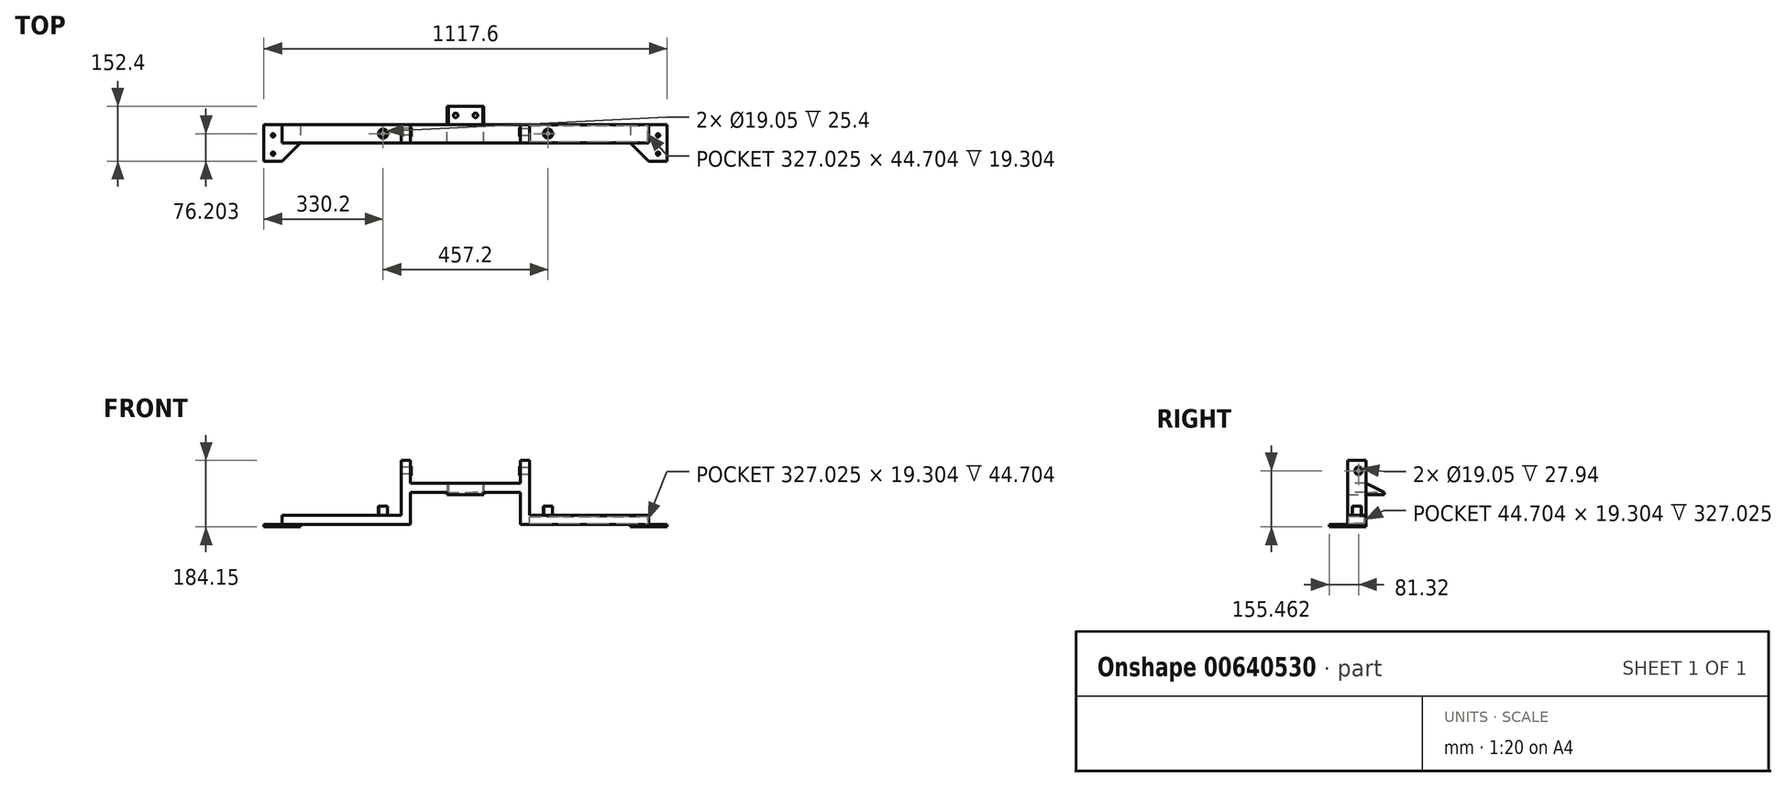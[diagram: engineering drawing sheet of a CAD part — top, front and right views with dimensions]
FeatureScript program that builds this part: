
annotation { "Feature Type Name" : "Feature", "Feature Type Description" : "" }
export const myFeature = defineFeature(function(context is Context, id is Id, definition is map)
    precondition{}
    {
        {
            var Q0;
            Q0=qCreatedBy(makeId("Top.planeOp"),FACE);
            var sketch = newSketch(context, id + "F0", { "sketchPlane" : qUnion([Q0])});
            skLineSegment(sketch, "E0.bottom", {"start": v(0, 37.2) * mm, "end": v(355.6, 37.2) * mm});
            skLineSegment(sketch, "E0.top", {"start": v(0, -13.6) * mm, "end": v(355.6, -13.6) * mm});
            skLineSegment(sketch, "E0.left", {"start": v(0, 37.2) * mm, "end": v(0, -13.6) * mm});
            skLineSegment(sketch, "E0.right", {"start": v(355.6, 37.2) * mm, "end": v(355.6, -13.6) * mm});
            skSolve(sketch);
        }
        {
            var Q0;
            Q0=makeQuery(id+"F0.imprint","IMPRINT",FACE,{"disambiguationData":[TD([[makeQuery(id+"F0.imprint","IMPRINT",EDGE,{"derivedFrom":sQuery(id+"F0.wireOp",EDGE,"E0.bottom")}),-1.0]])]});
            extrude(context, id + "F1", {"entities" : qUnion([Q0]), "depth" : 25.4 * mm, "offsetDistance" : 25.4 * mm});
        }
        {
            var Q0;
            Q0=qCreatedBy(makeId("Top.planeOp"),FACE);
            var sketch = newSketch(context, id + "F2", { "sketchPlane" : qUnion([Q0])});
            skLineSegment(sketch, "E1.0", {"start": v(0, 37.2) * mm, "end": v(355.6, 37.2) * mm});
            skLineSegment(sketch, "E2.0", {"start": v(0, -13.6) * mm, "end": v(355.6, -13.6) * mm});
            skLineSegment(sketch, "E3", {"start": v(304.8, -13.6) * mm, "end": v(355.6, -64.4) * mm});
            skLineSegment(sketch, "E4", {"start": v(355.6, -64.4) * mm, "end": v(406.4, -64.4) * mm});
            skLineSegment(sketch, "E5", {"start": v(406.4, -64.4) * mm, "end": v(406.4, 37.2) * mm});
            skLineSegment(sketch, "E6", {"start": v(406.4, 37.2) * mm, "end": v(304.8, 37.2) * mm});
            skLineSegment(sketch, "E7", {"start": v(304.8, 37.2) * mm, "end": v(304.8, -13.6) * mm});
            skSolve(sketch);
        }
        {
            var Q0;
            Q0=qSketchRegion(id+"F2",true);
            extrude(context, id + "F3", {"entities" : qUnion([Q0]), "operationType" : NewBodyOperationType.ADD, "oppositeDirection" : true, "depth" : 6.35 * mm, "offsetDistance" : 25.4 * mm});
        }
        {
            var Q0;
            Q0=makeQuery(id+"F3.opExtrude","CAP_FACE",FACE,{"disambiguationData":[OSD([sQuery(id+"F2.wireOp",EDGE,"E3"),sQuery(id+"F2.wireOp",EDGE,"E4"),sQuery(id+"F2.wireOp",EDGE,"E5"),sQuery(id+"F2.wireOp",EDGE,"E6"),sQuery(id+"F2.wireOp",EDGE,"E7")])],"isStart":true});
            var sketch = newSketch(context, id + "F4", { "sketchPlane" : qUnion([Q0])});
            skCircle(sketch, "E8", {"center": v(381, -43.77) * mm, "radius": 4.76 * mm});
            skCircle(sketch, "E9", {"center": v(381, 7.03) * mm, "radius": 4.76 * mm});
            skSolve(sketch);
        }
        {
            var Q0;
            Q0=qSketchRegion(id+"F4",true);
            extrude(context, id + "F5", {"entities" : qUnion([Q0]), "operationType" : NewBodyOperationType.REMOVE, "oppositeDirection" : true, "depth" : 25.4 * mm, "offsetDistance" : 25.4 * mm});
        }
        {
            var Q0;
            Q0=makeQuery(id+"F1.opExtrude","CAP_FACE",FACE,{"disambiguationData":[OSD([sQuery(id+"F0.wireOp",EDGE,"E0.bottom"),sQuery(id+"F0.wireOp",EDGE,"E0.top"),sQuery(id+"F0.wireOp",EDGE,"E0.left"),sQuery(id+"F0.wireOp",EDGE,"E0.right")])],"isStart":false});
            var sketch = newSketch(context, id + "F6", { "sketchPlane" : qUnion([Q0])});
            skCircle(sketch, "E10", {"center": v(76.2, 11.8) * mm, "radius": 12.7 * mm});
            skCircle(sketch, "E11", {"center": v(76.2, 11.8) * mm, "radius": 9.53 * mm});
            skSolve(sketch);
        }
        {
            var Q0;
            Q0=makeQuery(id+"F6.imprint","IMPRINT",FACE,{"disambiguationData":[TD([[makeQuery(id+"F6.imprint","IMPRINT",EDGE,{"derivedFrom":sQuery(id+"F6.wireOp",EDGE,"E10")}),1.0]])]});
            var Q1;
            Q1=sQuery(id+"F6.wireOp",EDGE,"E10");
            var Q2;
            Q2=sQuery(id+"F6.wireOp",EDGE,"E11");
            extrude(context, id + "F7", {"entities" : qUnion([Q0]), "operationType" : NewBodyOperationType.ADD, "surfaceEntities" : qUnion([Q1, Q2]), "depth" : 25.4 * mm, "offsetDistance" : 25.4 * mm});
        }
        {
            var Q0;
            Q0=makeQuery(id+"F1.opExtrude","CAP_FACE",FACE,{"disambiguationData":[OSD([sQuery(id+"F0.wireOp",EDGE,"E0.bottom"),sQuery(id+"F0.wireOp",EDGE,"E0.top"),sQuery(id+"F0.wireOp",EDGE,"E0.left"),sQuery(id+"F0.wireOp",EDGE,"E0.right")])],"isStart":false});
            var sketch = newSketch(context, id + "F8", { "sketchPlane" : qUnion([Q0])});
            skLineSegment(sketch, "E12.bottom", {"start": v(0, 37.2) * mm, "end": v(25.4, 37.2) * mm});
            skLineSegment(sketch, "E12.top", {"start": v(0, -13.6) * mm, "end": v(25.4, -13.6) * mm});
            skLineSegment(sketch, "E12.left", {"start": v(0, 37.2) * mm, "end": v(0, -13.6) * mm});
            skLineSegment(sketch, "E12.right", {"start": v(25.4, 37.2) * mm, "end": v(25.4, -13.6) * mm});
            skSolve(sketch);
        }
        {
            var Q0;
            Q0=qSketchRegion(id+"F8",true);
            extrude(context, id + "F9", {"entities" : qUnion([Q0]), "operationType" : NewBodyOperationType.ADD, "depth" : 152.4 * mm, "offsetDistance" : 25.4 * mm});
        }
        {
            var Q0;
            Q0=makeQuery(id+"F9.boolean.opBoolean","MERGE",FACE,{"derivedFrom":[makeQuery(id+"F1.opExtrude","SWEPT_FACE",FACE,{"disambiguationData":[OSD([sQuery(id+"F0.wireOp",EDGE,"E0.left")])]}),makeQuery(id+"F9.opExtrude","SWEPT_FACE",FACE,{"disambiguationData":[OSD([sQuery(id+"F8.wireOp",EDGE,"E12.left")])]})]});
            var sketch = newSketch(context, id + "F10", { "sketchPlane" : qUnion([Q0])});
            skLineSegment(sketch, "E13.bottom", {"start": v(-37.2, 114.3) * mm, "end": v(13.6, 114.3) * mm});
            skLineSegment(sketch, "E13.top", {"start": v(-37.2, 88.9) * mm, "end": v(13.6, 88.9) * mm});
            skLineSegment(sketch, "E13.left", {"start": v(-37.2, 114.3) * mm, "end": v(-37.2, 88.9) * mm});
            skLineSegment(sketch, "E13.right", {"start": v(13.6, 114.3) * mm, "end": v(13.6, 88.9) * mm});
            skSolve(sketch);
        }
        {
            var Q0;
            Q0=qSketchRegion(id+"F10",true);
            extrude(context, id + "F11", {"entities" : qUnion([Q0]), "operationType" : NewBodyOperationType.ADD, "depth" : 152.4 * mm, "offsetDistance" : 25.4 * mm});
        }
        {
            var Q0;
            {var subQ1=sQuery(id+"F8.wireOp",EDGE,"E12.left");Q0=makeQuery(id+"F11.boolean.opBoolean","SPLIT",FACE,{"disambiguationData":[TD([makeQuery(id+"F11.opExtrude","SWEPT_FACE",FACE,{"disambiguationData":[OSD([sQuery(id+"F10.wireOp",EDGE,"E13.bottom")])]})])],"derivedFrom":makeQuery(id+"F9.boolean.opBoolean","MERGE",FACE,{"derivedFrom":[makeQuery(id+"F1.opExtrude","SWEPT_FACE",FACE,{"disambiguationData":[OSD([sQuery(id+"F0.wireOp",EDGE,"E0.left")])]}),makeQuery(id+"F9.opExtrude","SWEPT_FACE",FACE,{"disambiguationData":[OSD([subQ1])]})]})});}
            var sketch = newSketch(context, id + "F12", { "sketchPlane" : qUnion([Q0])});
            skCircle(sketch, "E14", {"center": v(-16.9, 149.11) * mm, "radius": 12.7 * mm});
            skCircle(sketch, "E15", {"center": v(-16.9, 149.11) * mm, "radius": 9.53 * mm});
            skSolve(sketch);
        }
        {
            var Q0;
            Q0=qSketchRegion(id+"F12",true);
            extrude(context, id + "F13", {"entities" : qUnion([Q0]), "operationType" : NewBodyOperationType.ADD, "depth" : 2.54 * mm, "offsetDistance" : 25.4 * mm});
        }
        {
            var Q0;
            {var subQ1=sQuery(id+"F8.wireOp",EDGE,"E12.left");Q0=makeQuery(id+"F13.boolean.opBoolean","SPLIT",FACE,{"disambiguationData":[TD([makeQuery(id+"F13.opExtrude","SWEPT_FACE",FACE,{"disambiguationData":[OSD([sQuery(id+"F12.wireOp",EDGE,"E15")])]})])],"derivedFrom":makeQuery(id+"F11.boolean.opBoolean","SPLIT",FACE,{"disambiguationData":[TD([makeQuery(id+"F11.opExtrude","SWEPT_FACE",FACE,{"disambiguationData":[OSD([sQuery(id+"F10.wireOp",EDGE,"E13.bottom")])]})])],"derivedFrom":makeQuery(id+"F9.boolean.opBoolean","MERGE",FACE,{"derivedFrom":[makeQuery(id+"F1.opExtrude","SWEPT_FACE",FACE,{"disambiguationData":[OSD([sQuery(id+"F0.wireOp",EDGE,"E0.left")])]}),makeQuery(id+"F9.opExtrude","SWEPT_FACE",FACE,{"disambiguationData":[OSD([subQ1])]})]})})});}
            var sketch = newSketch(context, id + "F14", { "sketchPlane" : qUnion([Q0])});
            skCircle(sketch, "E16", {"center": v(-16.9, 149.11) * mm, "radius": 9.53 * mm});
            skSolve(sketch);
        }
        {
            var Q0;
            Q0=qSketchRegion(id+"F14",true);
            extrude(context, id + "F15", {"entities" : qUnion([Q0]), "operationType" : NewBodyOperationType.REMOVE, "oppositeDirection" : true, "depth" : 25.4 * mm, "offsetDistance" : 25.4 * mm});
        }
        {
            var Q0;
            Q0=makeQuery(id+"F11.opExtrude","SWEPT_FACE",FACE,{"disambiguationData":[OSD([sQuery(id+"F10.wireOp",EDGE,"E13.top")])]});
            var sketch = newSketch(context, id + "F16", { "sketchPlane" : qUnion([Q0])});
            skLineSegment(sketch, "E17.bottom", {"start": v(-101.6, 13.6) * mm, "end": v(-152.4, 13.6) * mm});
            skLineSegment(sketch, "E17.top", {"start": v(-101.6, -88) * mm, "end": v(-152.4, -88) * mm});
            skLineSegment(sketch, "E17.left", {"start": v(-101.6, 13.6) * mm, "end": v(-101.6, -88) * mm});
            skLineSegment(sketch, "E17.right", {"start": v(-152.4, 13.6) * mm, "end": v(-152.4, -88) * mm});
            skSolve(sketch);
        }
        {
            var Q0;
            Q0=qSketchRegion(id+"F16",true);
            extrude(context, id + "F17", {"entities" : qUnion([Q0]), "operationType" : NewBodyOperationType.ADD, "depth" : 6.35 * mm, "offsetDistance" : 25.4 * mm});
        }
        {
            var Q0;
            Q0=makeQuery(id+"F17.opExtrude","CAP_FACE",FACE,{"disambiguationData":[OSD([sQuery(id+"F16.wireOp",EDGE,"E17.bottom"),sQuery(id+"F16.wireOp",EDGE,"E17.top"),sQuery(id+"F16.wireOp",EDGE,"E17.left"),sQuery(id+"F16.wireOp",EDGE,"E17.right")])],"isStart":true});
            var sketch = newSketch(context, id + "F18", { "sketchPlane" : qUnion([Q0])});
            skCircle(sketch, "E18", {"center": v(-124.95, 62.6) * mm, "radius": 6.35 * mm});
            skPoint(sketch, "E18.centerSnap0", {"position": v(-101.6, 62.6) * mm});
            skSolve(sketch);
        }
        {
            var Q0;
            Q0=qSketchRegion(id+"F18",true);
            extrude(context, id + "F19", {"entities" : qUnion([Q0]), "operationType" : NewBodyOperationType.REMOVE, "oppositeDirection" : true, "depth" : 25.4 * mm, "offsetDistance" : 25.4 * mm});
        }
        {
            var Q0;
            Q0=makeQuery(id+"F17.opExtrude","SWEPT_FACE",FACE,{"disambiguationData":[OSD([sQuery(id+"F16.wireOp",EDGE,"E17.left")])]});
            var sketch = newSketch(context, id + "F20", { "sketchPlane" : qUnion([Q0])});
            skLineSegment(sketch, "E19", {"start": v(88, 88.9) * mm, "end": v(37.2, 114.3) * mm});
            skLineSegment(sketch, "E20", {"start": v(37.2, 114.3) * mm, "end": v(37.2, 82.55) * mm});
            skLineSegment(sketch, "E21", {"start": v(37.2, 82.55) * mm, "end": v(88, 82.55) * mm});
            skLineSegment(sketch, "E22", {"start": v(88, 82.55) * mm, "end": v(37.2, 82.55) * mm});
            skSolve(sketch);
        }
        {
            var Q0;
            {var subQ0=sQuery(id+"F20.wireOp",EDGE,"E19");Q0=makeQuery(id+"F20.imprint","IMPRINT",FACE,{"disambiguationData":[TD([[makeQuery(id+"F20.imprint","IMPRINT",EDGE,{"derivedFrom":subQ0}),1.0]])]});}
            var Q1;
            {var subQ6=sQuery(id+"F20.wireOp",EDGE,"E22");Q1=makeQuery(id+"F20.imprint","IMPRINT",FACE,{"disambiguationData":[TD([[makeQuery(id+"F20.imprint","IMPRINT",EDGE,{"derivedFrom":subQ6}),1.0]])]});}
            extrude(context, id + "F21", {"entities" : qUnion([Q0, Q1]), "operationType" : NewBodyOperationType.ADD, "oppositeDirection" : true, "depth" : 3.17 * mm, "offsetDistance" : 25.4 * mm});
        }
        {
            var Q0;
            Q0=makeQuery(id+"F1.opExtrude","SWEPT_BODY",BODY,{"disambiguationData":[OSD([sQuery(id+"F0.wireOp",EDGE,"E0.bottom"),sQuery(id+"F0.wireOp",EDGE,"E0.top"),sQuery(id+"F0.wireOp",EDGE,"E0.left"),sQuery(id+"F0.wireOp",EDGE,"E0.right")])]});
            var Q1;
            Q1=makeQuery(id+"F17.boolean.opBoolean","MERGE",FACE,{"derivedFrom":[makeQuery(id+"F11.opExtrude","CAP_FACE",FACE,{"disambiguationData":[OSD([sQuery(id+"F10.wireOp",EDGE,"E13.bottom"),sQuery(id+"F10.wireOp",EDGE,"E13.top"),sQuery(id+"F10.wireOp",EDGE,"E13.left"),sQuery(id+"F10.wireOp",EDGE,"E13.right")])],"isStart":false}),makeQuery(id+"F17.opExtrude","SWEPT_FACE",FACE,{"disambiguationData":[OSD([sQuery(id+"F16.wireOp",EDGE,"E17.right")])]})]});
            mirror(context, id + "F22", {"operationType" : NewBodyOperationType.ADD, "entities" : qUnion([Q0]), "mirrorPlane" : qUnion([Q1])});
        }
        {
            var Q0;
            Q0=makeQuery(id+"F1.opExtrude","SWEPT_FACE",FACE,{"disambiguationData":[OSD([sQuery(id+"F0.wireOp",EDGE,"E0.right")])]});
            cPlane(context, id + "F23", {"entities" : qUnion([Q0]), "cplaneType" : CPlaneType.OFFSET, "offset" : 3.17 * mm, "oppositeDirection" : true, "width" : 152.4 * mm, "height" : 152.4 * mm});
        }
        {
            var Q0;
            Q0=qCreatedBy(id+"F23.planeOp",FACE);
            var sketch = newSketch(context, id + "F24", { "sketchPlane" : qUnion([Q0])});
            skLineSegment(sketch, "E23.bottom", {"start": v(-10.56, 22.35) * mm, "end": v(34.15, 22.35) * mm});
            skLineSegment(sketch, "E23.top", {"start": v(-10.56, 3.05) * mm, "end": v(34.15, 3.05) * mm});
            skLineSegment(sketch, "E23.left", {"start": v(-10.56, 22.35) * mm, "end": v(-10.56, 3.05) * mm});
            skLineSegment(sketch, "E23.right", {"start": v(34.15, 22.35) * mm, "end": v(34.15, 3.05) * mm});
            skSolve(sketch);
        }
        {
            var Q0;
            Q0 = qSketchRegion(id + "F24", true);
            var Q1;
            Q1=makeQuery(id+"F9.opExtrude","SWEPT_FACE",FACE,{"disambiguationData":[OSD([sQuery(id+"F8.wireOp",EDGE,"E12.right")])]});
            extrude(context, id + "F25", {"entities" : qUnion([Q0]), "operationType" : NewBodyOperationType.REMOVE, "endBound" : BoundingType.UP_TO_SURFACE, "oppositeDirection" : true, "depth" : 25.4 * mm, "endBoundEntityFace" : qUnion([Q1]), "offsetDistance" : 25.4 * mm});
        }
    });
